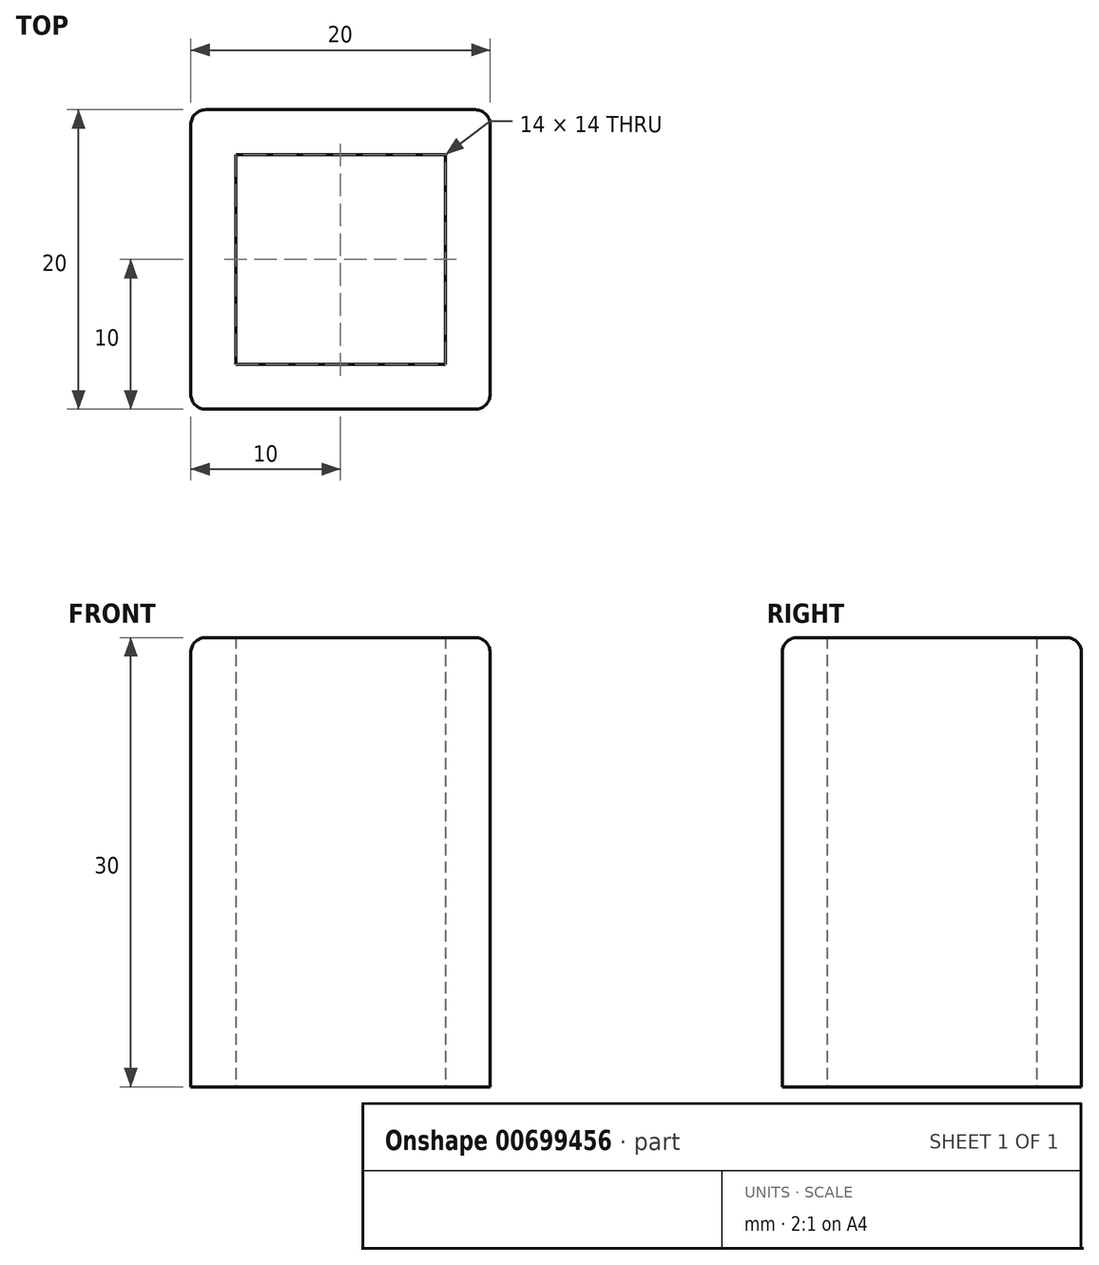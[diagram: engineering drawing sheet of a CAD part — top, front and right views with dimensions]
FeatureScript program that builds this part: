
annotation { "Feature Type Name" : "Feature", "Feature Type Description" : "" }
export const myFeature = defineFeature(function(context is Context, id is Id, definition is map)
    precondition{}
    {
        {
            var Q0;
            Q0=qCreatedBy(makeId("Top.planeOp"),FACE);
            var sketch = newSketch(context, id + "F0", { "sketchPlane" : qUnion([Q0])});
            skLineSegment(sketch, "E0.bottom", {"start": v(10, 10) * mm, "end": v(-10, 10) * mm});
            skLineSegment(sketch, "E0.top", {"start": v(10, -10) * mm, "end": v(-10, -10) * mm});
            skLineSegment(sketch, "E0.left", {"start": v(10, 10) * mm, "end": v(10, -10) * mm});
            skLineSegment(sketch, "E0.right", {"start": v(-10, 10) * mm, "end": v(-10, -10) * mm});
            skPoint(sketch, "E0.middle", {"position": v(0, 0) * mm});
            skLineSegment(sketch, "E1.0", {"start": v(7, -7) * mm, "end": v(-7, -7) * mm});
            skLineSegment(sketch, "E1.1", {"start": v(7, 7) * mm, "end": v(7, -7) * mm});
            skLineSegment(sketch, "E1.2", {"start": v(7, 7) * mm, "end": v(-7, 7) * mm});
            skLineSegment(sketch, "E1.3", {"start": v(-7, 7) * mm, "end": v(-7, -7) * mm});
            skSolve(sketch);
        }
        {
            var Q0;
            Q0=qSketchRegion(id+"F0",true);
            extrude(context, id + "F1", {"entities" : qUnion([Q0]), "depth" : 30 * mm, "offsetDistance" : 25 * mm});
        }
        {
            var Q0;
            Q0=makeQuery(id+"F1.opExtrude","SWEPT_EDGE",EDGE,{"disambiguationData":[OSD([sQuery(id+"F0.wireOp",EDGE,"E0.top"),sQuery(id+"F0.wireOp",EDGE,"E0.right")])]});
            var Q1;
            Q1=makeQuery(id+"F1.opExtrude","CAP_EDGE",EDGE,{"disambiguationData":[OSD([sQuery(id+"F0.wireOp",EDGE,"E0.top")])],"isStart":false});
            var Q2;
            Q2=makeQuery(id+"F1.opExtrude","SWEPT_EDGE",EDGE,{"disambiguationData":[OSD([sQuery(id+"F0.wireOp",EDGE,"E0.top"),sQuery(id+"F0.wireOp",EDGE,"E0.left")])]});
            var Q3;
            Q3=makeQuery(id+"F1.opExtrude","CAP_EDGE",EDGE,{"disambiguationData":[OSD([sQuery(id+"F0.wireOp",EDGE,"E0.left")])],"isStart":false});
            var Q4;
            Q4=makeQuery(id+"F1.opExtrude","SWEPT_EDGE",EDGE,{"disambiguationData":[OSD([sQuery(id+"F0.wireOp",EDGE,"E0.bottom"),sQuery(id+"F0.wireOp",EDGE,"E0.left")])]});
            var Q5;
            Q5=makeQuery(id+"F1.opExtrude","CAP_EDGE",EDGE,{"disambiguationData":[OSD([sQuery(id+"F0.wireOp",EDGE,"E0.bottom")])],"isStart":false});
            var Q6;
            Q6=makeQuery(id+"F1.opExtrude","CAP_EDGE",EDGE,{"disambiguationData":[OSD([sQuery(id+"F0.wireOp",EDGE,"E0.right")])],"isStart":false});
            var Q7;
            Q7=makeQuery(id+"F1.opExtrude","SWEPT_EDGE",EDGE,{"disambiguationData":[OSD([sQuery(id+"F0.wireOp",EDGE,"E0.bottom"),sQuery(id+"F0.wireOp",EDGE,"E0.right")])]});
            fillet(context, id + "F2", {"entities" : qUnion([Q0, Q1, Q2, Q3, Q4, Q5, Q6, Q7]), "radius" : 1 * mm, "tangentPropagation" : true, "allowEdgeOverflow" : false});
        }
    });
